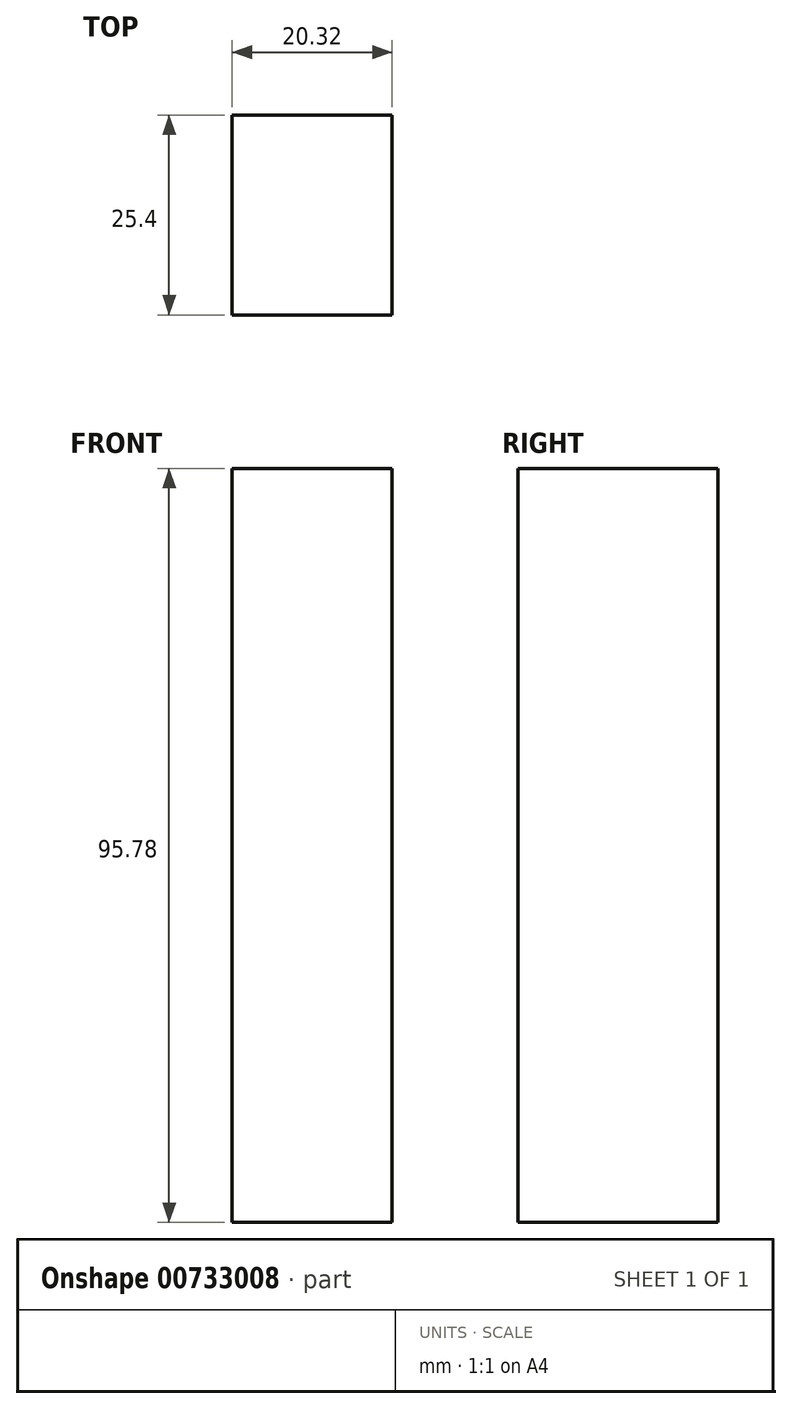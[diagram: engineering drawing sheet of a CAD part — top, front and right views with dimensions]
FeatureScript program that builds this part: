
annotation { "Feature Type Name" : "Feature", "Feature Type Description" : "" }
export const myFeature = defineFeature(function(context is Context, id is Id, definition is map)
    precondition{}
    {
        {
            var Q0;
            Q0=qCreatedBy(makeId("Right.planeOp"),FACE);
            var sketch = newSketch(context, id + "F0", { "sketchPlane" : qUnion([Q0])});
            skLineSegment(sketch, "E0.bottom", {"start": v(-50.7, 48.17) * mm, "end": v(-25.3, 48.17) * mm});
            skLineSegment(sketch, "E0.top", {"start": v(-50.7, -47.6) * mm, "end": v(-25.3, -47.6) * mm});
            skLineSegment(sketch, "E0.left", {"start": v(-50.7, 48.17) * mm, "end": v(-50.7, -47.6) * mm});
            skLineSegment(sketch, "E0.right", {"start": v(-25.3, 48.17) * mm, "end": v(-25.3, -47.6) * mm});
            skSolve(sketch);
        }
        {
            var Q0;
            Q0=makeQuery(id+"F0.imprint","IMPRINT",FACE,{"disambiguationData":[TD([[makeQuery(id+"F0.imprint","IMPRINT",EDGE,{"derivedFrom":sQuery(id+"F0.wireOp",EDGE,"E0.bottom")}),-1.0]])]});
            extrude(context, id + "F1", {"entities" : qUnion([Q0]), "depth" : 20.32 * mm, "offsetDistance" : 25.4 * mm});
        }
    });
